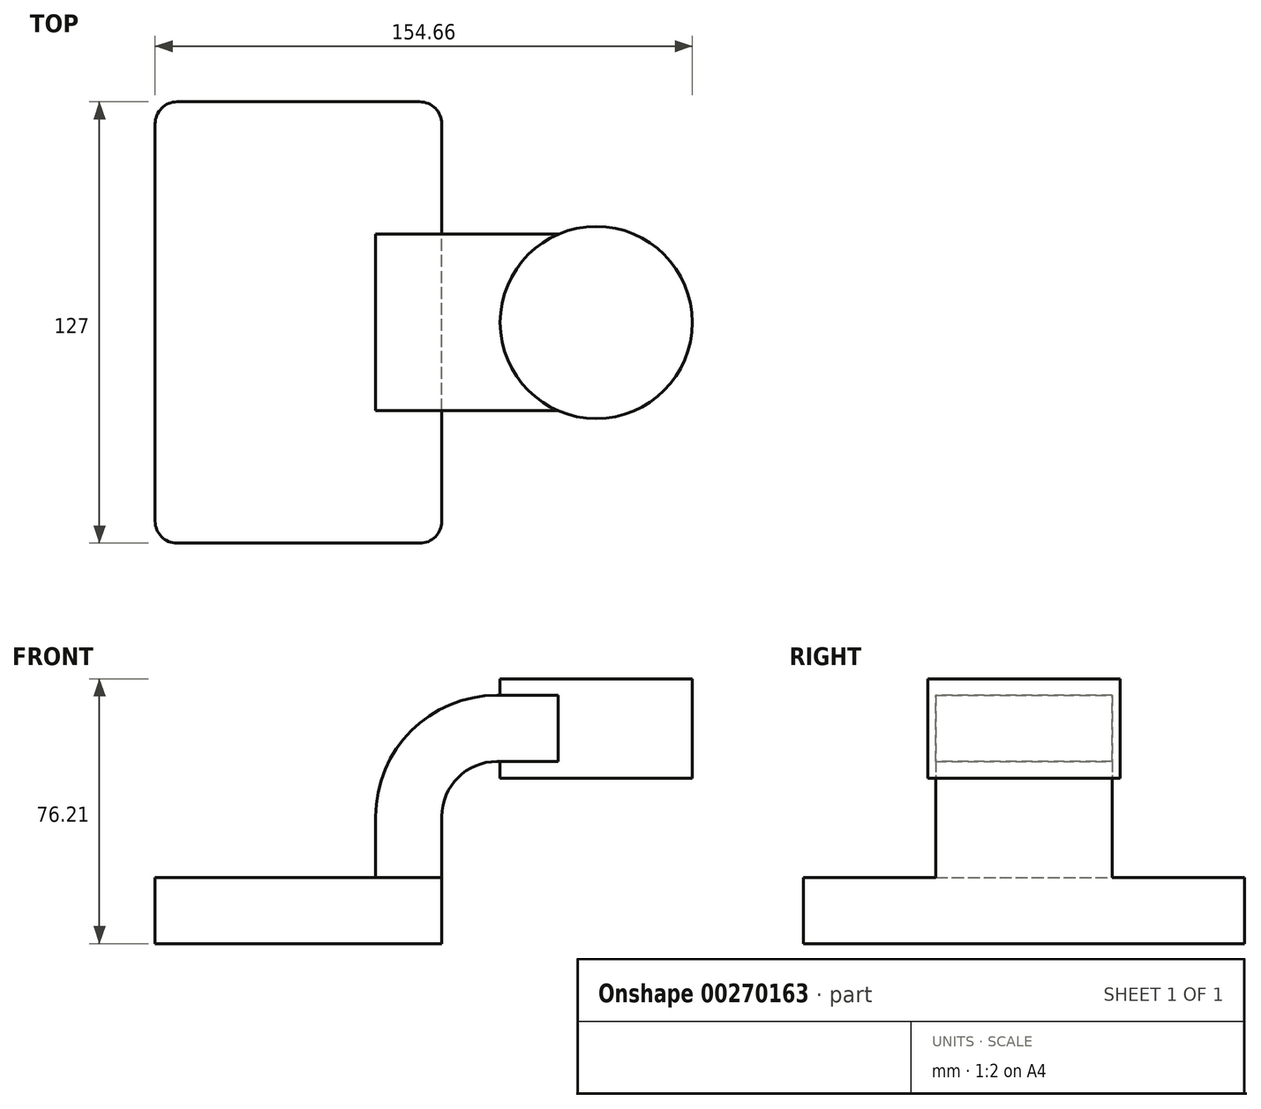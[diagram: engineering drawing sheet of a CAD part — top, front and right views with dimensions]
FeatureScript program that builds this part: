
annotation { "Feature Type Name" : "Feature", "Feature Type Description" : "" }
export const myFeature = defineFeature(function(context is Context, id is Id, definition is map)
    precondition{}
    {
        {
            var Q0;
            Q0=qCreatedBy(makeId("Front.planeOp"),FACE);
            var sketch = newSketch(context, id + "F0", { "sketchPlane" : qUnion([Q0])});
            skLineSegment(sketch, "E0.bottom", {"start": v(-41.28, -9.53) * mm, "end": v(41.28, -9.53) * mm});
            skLineSegment(sketch, "E0.top", {"start": v(-41.28, 9.53) * mm, "end": v(41.28, 9.53) * mm});
            skLineSegment(sketch, "E0.left", {"start": v(-41.28, -9.53) * mm, "end": v(-41.28, 9.53) * mm});
            skLineSegment(sketch, "E0.right", {"start": v(41.28, -9.53) * mm, "end": v(41.28, 9.53) * mm});
            skPoint(sketch, "E0.middle", {"position": v(0, 0) * mm});
            skLineSegment(sketch, "E1.bottom", {"start": v(113.39, 66.68) * mm, "end": v(62.59, 66.68) * mm});
            skLineSegment(sketch, "E1.top", {"start": v(113.39, 38.1) * mm, "end": v(62.59, 38.1) * mm});
            skLineSegment(sketch, "E1.left", {"start": v(113.39, 66.68) * mm, "end": v(113.39, 38.1) * mm});
            skLineSegment(sketch, "E1.right", {"start": v(62.59, 66.68) * mm, "end": v(62.59, 38.1) * mm});
            skPoint(sketch, "E1.middle", {"position": v(87.99, 52.39) * mm});
            skLineSegment(sketch, "E2", {"start": v(41.27, 9.52) * mm, "end": v(41.27, 27) * mm});
            skArc(sketch, "E3", {"start": v(41.27, 27) * mm, "mid": v(45.92, 38.23) * mm, "end": v(57.15, 42.88) * mm});
            skLineSegment(sketch, "E4", {"start": v(57.15, 42.88) * mm, "end": v(85.72, 42.88) * mm});
            skLineSegment(sketch, "E5.0", {"start": v(57.15, 61.93) * mm, "end": v(85.72, 61.93) * mm});
            skArc(sketch, "E5.1", {"start": v(22.22, 27) * mm, "mid": v(32.45, 51.7) * mm, "end": v(57.15, 61.93) * mm});
            skLineSegment(sketch, "E5.2", {"start": v(22.22, 9.52) * mm, "end": v(22.22, 27) * mm});
            skLineSegment(sketch, "E6", {"start": v(85.72, 66.68) * mm, "end": v(85.72, 38.1) * mm});
            skPoint(sketch, "E6.startSnap0", {"position": v(87.99, 66.68) * mm});
            skFitSpline(sketch, "E7", {"points": [v(-41.28, 9.53) * mm, v(57.15, 61.93) * mm], "startDerivative": vector(53.75, 88.92) * mm, "endDerivative": vector(171.45, -0.54) * mm});
            skSolve(sketch);
        }
        {
            var Q0;
            Q0=makeQuery(id+"F0.imprint","IMPRINT",FACE,{"disambiguationData":[TD([[makeQuery(id+"F0.imprint","IMPRINT",EDGE,{"derivedFrom":sQuery(id+"F0.wireOp",EDGE,"E0.bottom")}),1.0]])]});
            extrude(context, id + "F1", {"entities" : qUnion([Q0]), "endBound" : BoundingType.SYMMETRIC, "depth" : 127 * mm});
        }
        {
            var Q0;
            {var subQ1=sQuery(id+"F0.wireOp",EDGE,"E2");Q0=makeQuery(id+"F0.imprint","IMPRINT",FACE,{"disambiguationData":[TD([[makeQuery(id+"F0.imprint","IMPRINT",EDGE,{"derivedFrom":subQ1}),1.0]])]});}
            var Q1;
            {var subQ0=sQuery(id+"F0.wireOp",EDGE,"E5.0");var subQ1=sQuery(id+"F0.wireOp",EDGE,"E1.right");var subQ2=makeQuery(id+"F0.imprint","INTERSECT",VERTEX,{"derivedFrom":[subQ1,subQ0]});Q1=makeQuery(id+"F0.imprint","IMPRINT",FACE,{"disambiguationData":[TD([[makeQuery(id+"F0.imprint","IMPRINT",EDGE,{"disambiguationData":[TD([[subQ2,-1.0]])],"derivedFrom":subQ1}),1.0]])]});}
            extrude(context, id + "F2", {"entities" : qUnion([Q0, Q1]), "operationType" : NewBodyOperationType.ADD, "endBound" : BoundingType.SYMMETRIC, "depth" : 50.8 * mm});
        }
        {
            var Q0;
            Q0=makeQuery(id+"F0.imprint","IMPRINT",FACE,{"disambiguationData":[TD([[makeQuery(id+"F0.imprint","IMPRINT",EDGE,{"derivedFrom":sQuery(id+"F0.wireOp",EDGE,"E5.1")}),1.0]])]});
            extrude(context, id + "F3", {"entities" : qUnion([Q0]), "operationType" : NewBodyOperationType.ADD, "endBound" : BoundingType.SYMMETRIC, "depth" : 15.88 * mm});
        }
        {
            var Q0;
            {var subQ0=sQuery(id+"F0.wireOp",EDGE,"E1.left");Q0=makeQuery(id+"F0.imprint","IMPRINT",FACE,{"disambiguationData":[TD([[makeQuery(id+"F0.imprint","IMPRINT",EDGE,{"derivedFrom":subQ0}),-1.0]])]});}
            var Q1;
            Q1=sQuery(id+"F0.wireOp",EDGE,"E6");
            revolve(context, id + "F4", {"operationType" : NewBodyOperationType.ADD, "entities" : qUnion([Q0]), "axis" : qUnion([Q1]), "revolveType" : RevolveType.FULL});
        }
        {
            var Q0;
            Q0=makeQuery(id+"F1.opExtrude","CAP_EDGE",EDGE,{"disambiguationData":[OSD([sQuery(id+"F0.wireOp",EDGE,"E0.right")])],"isStart":true});
            var Q1;
            Q1=makeQuery(id+"F1.opExtrude","CAP_EDGE",EDGE,{"disambiguationData":[OSD([sQuery(id+"F0.wireOp",EDGE,"E0.left")])],"isStart":true});
            var Q2;
            Q2=makeQuery(id+"F1.opExtrude","CAP_EDGE",EDGE,{"disambiguationData":[OSD([sQuery(id+"F0.wireOp",EDGE,"E0.left")])],"isStart":false});
            var Q3;
            Q3=makeQuery(id+"F1.opExtrude","CAP_EDGE",EDGE,{"disambiguationData":[OSD([sQuery(id+"F0.wireOp",EDGE,"E0.right")])],"isStart":false});
            fillet(context, id + "F5", {"entities" : qUnion([Q0, Q1, Q2, Q3]), "radius" : 6.35 * mm, "tangentPropagation" : true, "allowEdgeOverflow" : false});
        }
    });
